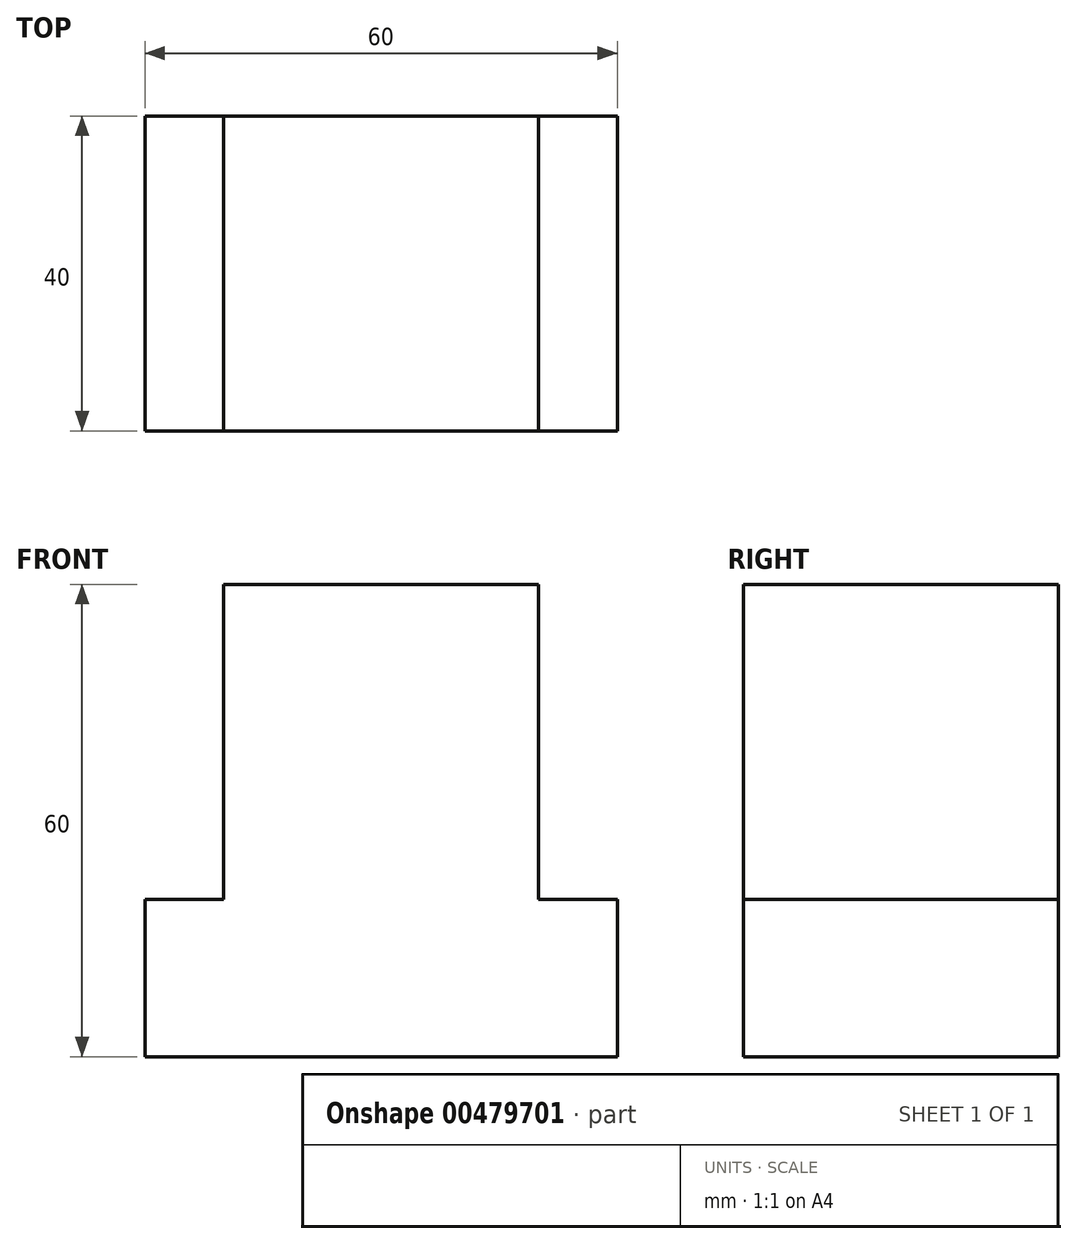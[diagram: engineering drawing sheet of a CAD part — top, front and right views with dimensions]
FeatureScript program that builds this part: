
annotation { "Feature Type Name" : "Feature", "Feature Type Description" : "" }
export const myFeature = defineFeature(function(context is Context, id is Id, definition is map)
    precondition{}
    {
        {
            var Q0;
            Q0=qCreatedBy(makeId("Front.planeOp"),FACE);
            var sketch = newSketch(context, id + "F0", { "sketchPlane" : qUnion([Q0])});
            skLineSegment(sketch, "E0.bottom", {"start": v(0, 0) * mm, "end": v(60, 0) * mm});
            skLineSegment(sketch, "E0.top", {"start": v(0, 20) * mm, "end": v(60, 20) * mm});
            skLineSegment(sketch, "E0.left", {"start": v(0, 0) * mm, "end": v(0, 20) * mm});
            skLineSegment(sketch, "E0.right", {"start": v(60, 0) * mm, "end": v(60, 20) * mm});
            skLineSegment(sketch, "E1", {"start": v(0, 20) * mm, "end": v(10, 20) * mm});
            skLineSegment(sketch, "E2", {"start": v(10, 20) * mm, "end": v(10, 60) * mm});
            skLineSegment(sketch, "E3", {"start": v(10, 60) * mm, "end": v(50, 60) * mm});
            skLineSegment(sketch, "E4", {"start": v(50, 60) * mm, "end": v(50, 20) * mm});
            skSolve(sketch);
        }
        {
            var Q0;
            Q0=qSketchRegion(id+"F0",true);
            extrude(context, id + "F1", {"entities" : qUnion([Q0]), "oppositeDirection" : true, "depth" : 40 * mm});
        }
    });
